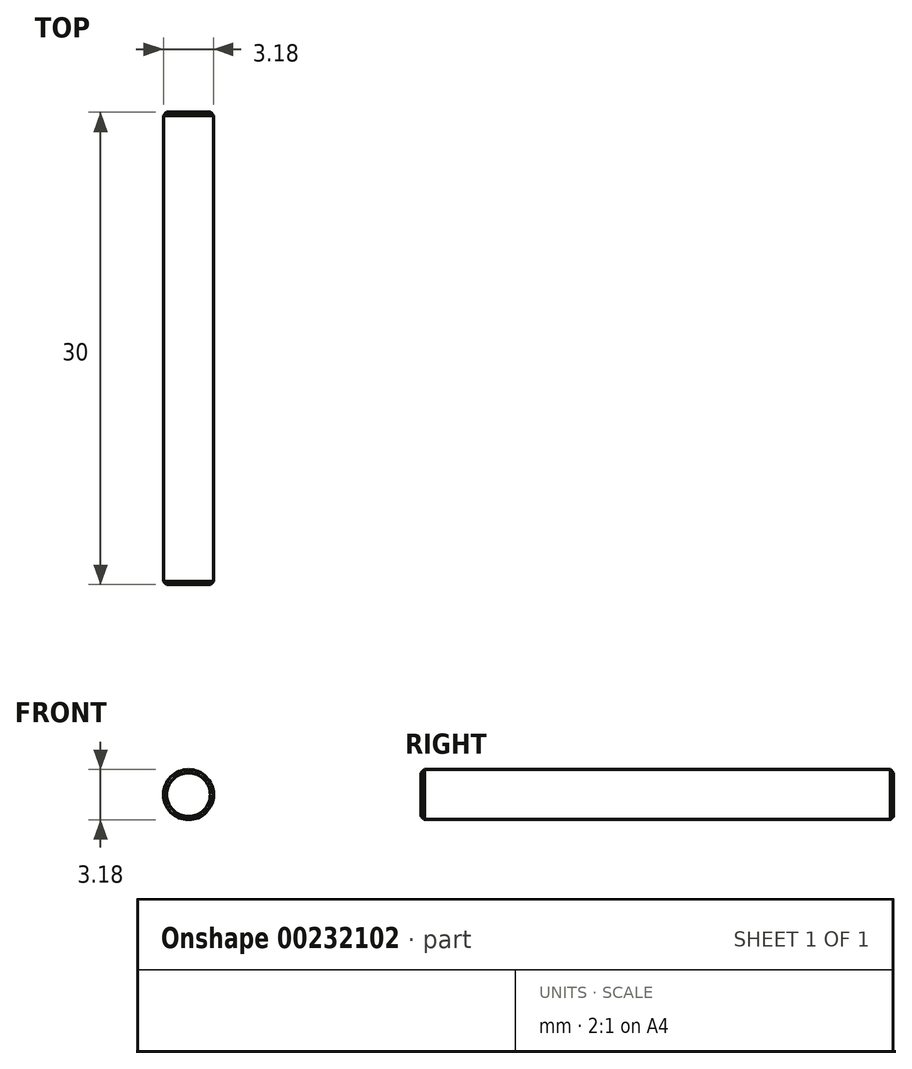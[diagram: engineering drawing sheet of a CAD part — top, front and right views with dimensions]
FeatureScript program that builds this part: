
annotation { "Feature Type Name" : "Feature", "Feature Type Description" : "" }
export const myFeature = defineFeature(function(context is Context, id is Id, definition is map)
    precondition{}
    {
        {
            var Q0;
            Q0=qCreatedBy(makeId("Front.planeOp"),FACE);
            var sketch = newSketch(context, id + "F0", { "sketchPlane" : qUnion([Q0])});
            skCircle(sketch, "E0", {"center": v(0, 0) * mm, "radius": 1.59 * mm});
            skSolve(sketch);
        }
        {
            var Q0;
            Q0 = qSketchRegion(id + "F0", true);
            extrude(context, id + "F1", {"entities" : qUnion([Q0]), "depth" : 30 * mm});
        }
        {
            var Q0;
            Q0=makeQuery(id+"F1.opExtrude","CAP_EDGE",EDGE,{"disambiguationData":[OSD([sQuery(id+"F0.wireOp",EDGE,"E0")])],"isStart":false});
            var Q1;
            Q1=makeQuery(id+"F1.opExtrude","CAP_EDGE",EDGE,{"disambiguationData":[OSD([sQuery(id+"F0.wireOp",EDGE,"E0")])],"isStart":true});
            chamfer(context, id + "F2", {"entities" : qUnion([Q0, Q1]), "width" : .2 * mm, "tangentPropagation" : true});
        }
    });
